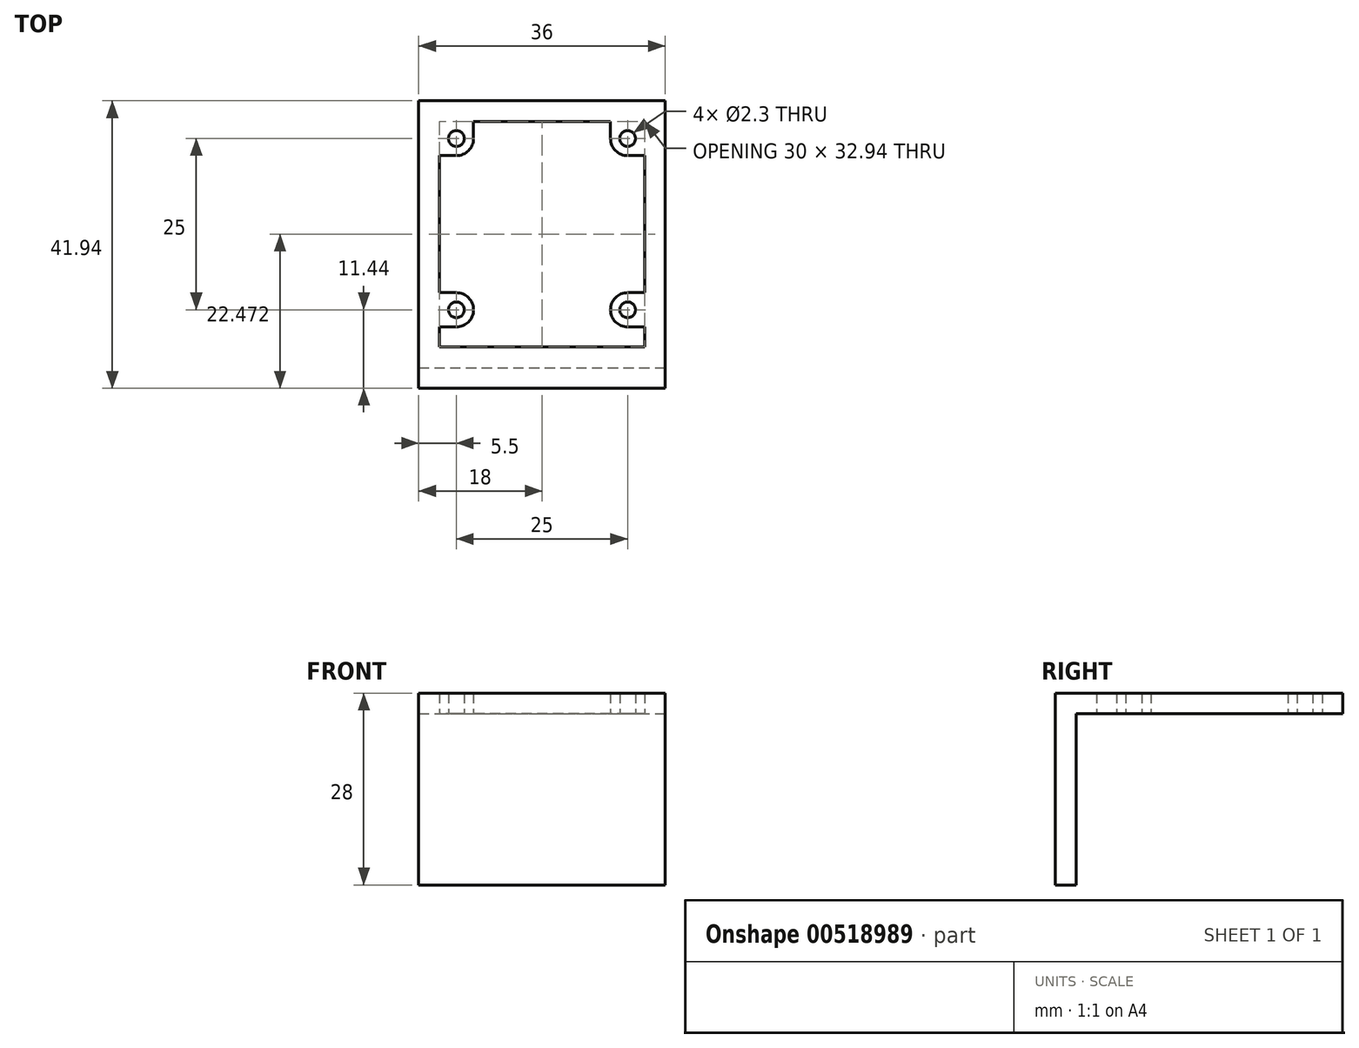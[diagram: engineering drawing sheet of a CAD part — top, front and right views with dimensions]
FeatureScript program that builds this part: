
annotation { "Feature Type Name" : "Feature", "Feature Type Description" : "" }
export const myFeature = defineFeature(function(context is Context, id is Id, definition is map)
    precondition{}
    {
        {
            var Q0;
            Q0=qCreatedBy(makeId("Top.planeOp"),FACE);
            var sketch = newSketch(context, id + "F0", { "sketchPlane" : qUnion([Q0])});
            skLineSegment(sketch, "E0.bottom", {"start": v(-18, 18) * mm, "end": v(18, 18) * mm});
            skLineSegment(sketch, "E0.top", {"start": v(-18, -23.94) * mm, "end": v(18, -23.94) * mm});
            skLineSegment(sketch, "E0.left", {"start": v(-18, 18) * mm, "end": v(-18, -23.94) * mm});
            skLineSegment(sketch, "E0.right", {"start": v(18, 18) * mm, "end": v(18, -23.94) * mm});
            skCircle(sketch, "E1", {"center": v(-12.5, 12.5) * mm, "radius": 1.15 * mm});
            skCircle(sketch, "E2", {"center": v(-12.5, -12.5) * mm, "radius": 1.15 * mm});
            skCircle(sketch, "E3", {"center": v(12.5, -12.5) * mm, "radius": 1.15 * mm});
            skCircle(sketch, "E4", {"center": v(12.5, 12.5) * mm, "radius": 1.15 * mm});
            skLineSegment(sketch, "E5", {"start": v(-12.5, 12.5) * mm, "end": v(12.5, -12.5) * mm, "construction": true});
            skLineSegment(sketch, "E6", {"start": v(-12.5, -12.5) * mm, "end": v(12.5, 12.5) * mm, "construction": true});
            skLineSegment(sketch, "E7", {"start": v(-12.5, 10) * mm, "end": v(-15, 10) * mm});
            skLineSegment(sketch, "E8", {"start": v(-15, 10) * mm, "end": v(-15, -10) * mm});
            skLineSegment(sketch, "E9", {"start": v(-15, -10) * mm, "end": v(-12.5, -10) * mm});
            skLineSegment(sketch, "E10", {"start": v(-10, -12.5) * mm, "end": v(-10, -12.5) * mm});
            skLineSegment(sketch, "E11", {"start": v(-12.5, -15) * mm, "end": v(-15, -15) * mm});
            skLineSegment(sketch, "E12", {"start": v(-15, -15) * mm, "end": v(-15, -17.94) * mm});
            skLineSegment(sketch, "E13", {"start": v(-15, -17.94) * mm, "end": v(15, -17.94) * mm});
            skLineSegment(sketch, "E14", {"start": v(15, -17.94) * mm, "end": v(15, -15) * mm});
            skLineSegment(sketch, "E15", {"start": v(15, -15) * mm, "end": v(12.5, -15) * mm});
            skLineSegment(sketch, "E16", {"start": v(10, -12.5) * mm, "end": v(10, -12.5) * mm});
            skLineSegment(sketch, "E17", {"start": v(12.5, -10) * mm, "end": v(15, -10) * mm});
            skLineSegment(sketch, "E18", {"start": v(15, -10) * mm, "end": v(15, 10) * mm});
            skLineSegment(sketch, "E19", {"start": v(15, 10) * mm, "end": v(12.5, 10) * mm});
            skLineSegment(sketch, "E20", {"start": v(10, 12.5) * mm, "end": v(10, 15) * mm});
            skLineSegment(sketch, "E21", {"start": v(10, 15) * mm, "end": v(-10, 15) * mm});
            skLineSegment(sketch, "E22", {"start": v(-10, 15) * mm, "end": v(-10, 12.5) * mm});
            skPoint(sketch, "E23.visualSharp", {"position": v(-10, 10) * mm});
            skArc(sketch, "E23.filletArc", {"start": v(-12.5, 10) * mm, "mid": v(-10.73, 10.73) * mm, "end": v(-10, 12.5) * mm});
            skPoint(sketch, "E24.visualSharp", {"position": v(10, 10) * mm});
            skArc(sketch, "E24.filletArc", {"start": v(10, 12.5) * mm, "mid": v(10.73, 10.73) * mm, "end": v(12.5, 10) * mm});
            skPoint(sketch, "E25.visualSharp", {"position": v(10, -10) * mm});
            skArc(sketch, "E25.filletArc", {"start": v(12.5, -10) * mm, "mid": v(10.73, -10.73) * mm, "end": v(10, -12.5) * mm});
            skPoint(sketch, "E26.visualSharp", {"position": v(-10, -10) * mm});
            skArc(sketch, "E26.filletArc", {"start": v(-10, -12.5) * mm, "mid": v(-10.73, -10.73) * mm, "end": v(-12.5, -10) * mm});
            skPoint(sketch, "E27.visualSharp", {"position": v(-10, -15) * mm});
            skArc(sketch, "E27.filletArc", {"start": v(-12.5, -15) * mm, "mid": v(-10.73, -14.27) * mm, "end": v(-10, -12.5) * mm});
            skPoint(sketch, "E28.visualSharp", {"position": v(10, -15) * mm});
            skArc(sketch, "E28.filletArc", {"start": v(10, -12.5) * mm, "mid": v(10.73, -14.27) * mm, "end": v(12.5, -15) * mm});
            skLineSegment(sketch, "E29.bottom", {"start": v(-18, -20.94) * mm, "end": v(18, -20.94) * mm});
            skLineSegment(sketch, "E29.left", {"start": v(-18, -20.94) * mm, "end": v(-18, -23.94) * mm});
            skLineSegment(sketch, "E29.right", {"start": v(18, -20.94) * mm, "end": v(18, -23.94) * mm});
            skSolve(sketch);
        }
        {
            var Q0;
            Q0=makeQuery(id+"F0.imprint","IMPRINT",FACE,{"disambiguationData":[TD([[makeQuery(id+"F0.imprint","IMPRINT",EDGE,{"derivedFrom":sQuery(id+"F0.wireOp",EDGE,"E0.bottom")}),-1.0]])]});
            var Q1;
            Q1=makeQuery(id+"F0.imprint","IMPRINT",FACE,{"disambiguationData":[TD([[makeQuery(id+"F0.imprint","IMPRINT",EDGE,{"derivedFrom":sQuery(id+"F0.wireOp",EDGE,"E29.bottom")}),-1.0]])]});
            extrude(context, id + "F1", {"entities" : qUnion([Q0, Q1]), "depth" : 3 * mm, "offsetDistance" : 25 * mm});
        }
        {
            var Q0;
            Q0=makeQuery(id+"F0.imprint","IMPRINT",FACE,{"disambiguationData":[TD([[makeQuery(id+"F0.imprint","IMPRINT",EDGE,{"derivedFrom":sQuery(id+"F0.wireOp",EDGE,"E29.bottom")}),-1.0]])]});
            extrude(context, id + "F2", {"entities" : qUnion([Q0]), "operationType" : NewBodyOperationType.ADD, "oppositeDirection" : true, "depth" : 25 * mm, "offsetDistance" : 25 * mm});
        }
    });
